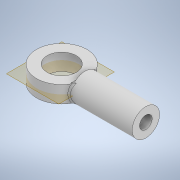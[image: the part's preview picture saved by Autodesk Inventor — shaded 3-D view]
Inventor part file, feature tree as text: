
AUTODESK INVENTOR PART (.ipt)
format: ipt  version: 2020 (Build 240168000, 168)  size: 224,768 bytes
history: native  units: mm
features: sketch x4, extrude x3, fillet x3, projected_geometry x3, thicken_offset x2, plane x1, revolve x1
ambient origin geometry x8: Origin, YZ Plane, XZ Plane, XY Plane, X Axis, Y Axis, Z Axis, Center Point
bodies: Solid1 (feature_tree)
feature tree (17):
  extrude  "Extrusion1"  Depth=4.0mm TaperAngle=0.0deg
  extrude  "Extrusion2"  Depth=20.0mm TaperAngle=0.0deg
  thicken_offset  "Thicken1"
  thicken_offset  "Thicken2"
  fillet  "Fillet1"  Radius=5.5mm
  fillet  "Fillet2"  Radius=5.5mm
  fillet  "Fillet3"  Radius=5.5mm
  extrude  "Extrusion3"  Depth=0.5mm
  plane  "Work Plane1"
  revolve  "Revolution1"  [1 undecoded]
  sketch  "Sketch1"  dims[d0=12.0mm d1=4.0mm d2=0.0mm]
  sketch  "Sketch2"  dims[d3=6.5mm d4=20.0mm d5=0.0mm d6=5.5mm d7=5.5mm d8=5.5mm]
  projected_geometry  "Projected Loop1"
  sketch  "Sketch3"  dims[d9=5.5mm d10=0.5mm]
  projected_geometry  "Projected Loop2"
  sketch  "Sketch4"  dims[d11=0.5mm d12=0.5mm d13=3.0mm d14=10.0mm d15=0.0mm d16=-2.0mm d17=8.0mm d18=90.0deg]
  projected_geometry  "Projected Loop3"
note: 1 required parameter value undecoded (feature->parameter linkage not recoverable at this tier; creation-order binding heuristic only, values carry confidence <= 0.55)
